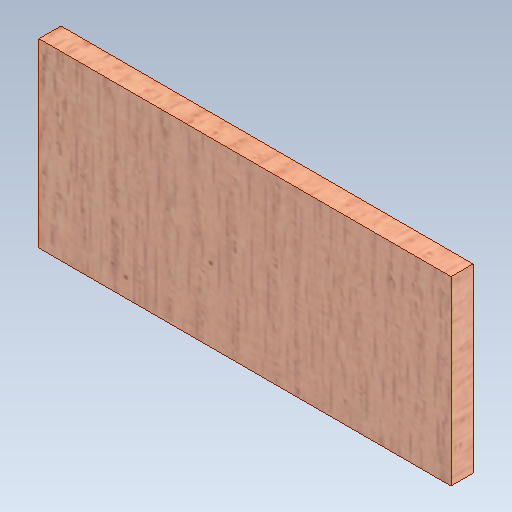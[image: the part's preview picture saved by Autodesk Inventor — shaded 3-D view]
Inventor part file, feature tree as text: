
AUTODESK INVENTOR PART (.ipt)
format: ipt  version: 2020 (Build 240168000, 168)  size: 250,368 bytes
history: native  units: mm
features: extrude x1, sketch x1
ambient origin geometry x8: Origin, YZ Plane, XZ Plane, XY Plane, X Axis, Y Axis, Z Axis, Center Point
bodies: Solid1 (feature_tree)
feature tree (2):
  extrude  "Extrusion1"  Depth=66.0mm
  sketch  "Sketch1"  dims[d0=150.0mm d1=66.0mm d2=8.0mm d3=0.0mm]
